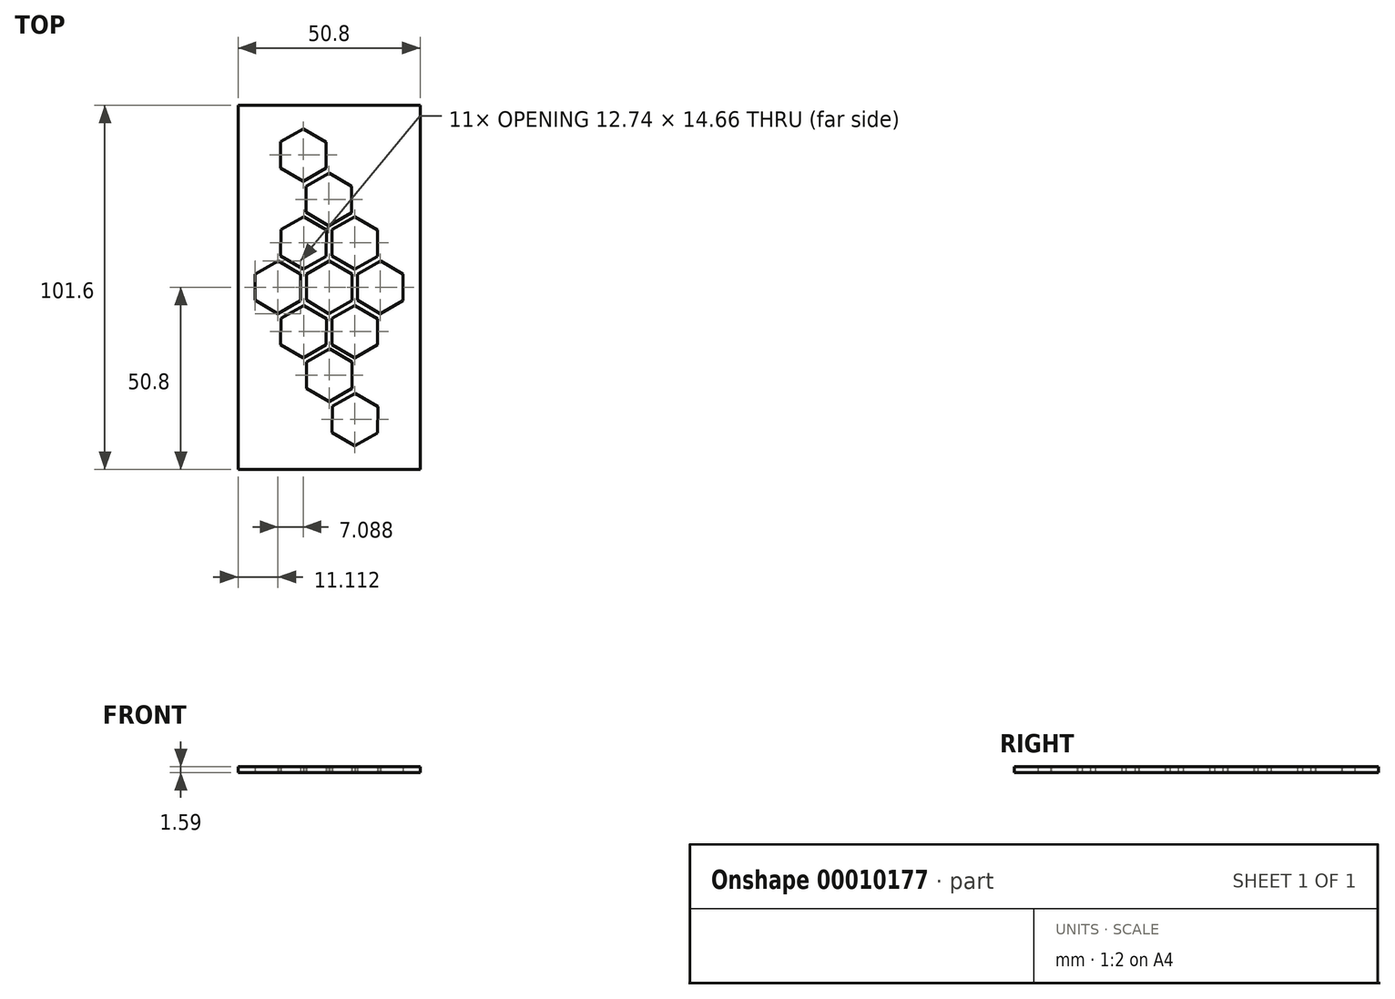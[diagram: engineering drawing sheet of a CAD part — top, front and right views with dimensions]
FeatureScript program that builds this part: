
annotation { "Feature Type Name" : "Feature", "Feature Type Description" : "" }
export const myFeature = defineFeature(function(context is Context, id is Id, definition is map)
    precondition{}
    {
        {
            var Q0;
            Q0=qCreatedBy(makeId("Top.planeOp"),FACE);
            var sketch = newSketch(context, id + "F0", { "sketchPlane" : qUnion([Q0])});
            skLineSegment(sketch, "E0.rect.bottom", {"start": v(25.4, 50.8) * mm, "end": v(-25.4, 50.8) * mm});
            skLineSegment(sketch, "E0.rect.top", {"start": v(25.4, -50.8) * mm, "end": v(-25.4, -50.8) * mm});
            skLineSegment(sketch, "E0.rect.left", {"start": v(25.4, 50.8) * mm, "end": v(25.4, -50.8) * mm});
            skLineSegment(sketch, "E0.rect.right", {"start": v(-25.4, 50.8) * mm, "end": v(-25.4, -50.8) * mm});
            skPoint(sketch, "E0.rect.middle", {"position": v(0, 0) * mm});
            skCircle(sketch, "E1.cCircle", {"center": v(0, 0) * mm, "radius": 6.35 * mm, "construction": true});
            skLineSegment(sketch, "E1.0", {"start": v(0.04, 7.33) * mm, "end": v(6.37, 3.63) * mm});
            skLineSegment(sketch, "E1.1", {"start": v(6.37, 3.63) * mm, "end": v(6.33, -3.7) * mm});
            skLineSegment(sketch, "E1.2", {"start": v(6.33, -3.7) * mm, "end": v(-0.04, -7.33) * mm});
            skLineSegment(sketch, "E1.3", {"start": v(-0.04, -7.33) * mm, "end": v(-6.37, -3.63) * mm});
            skLineSegment(sketch, "E1.4", {"start": v(-6.37, -3.63) * mm, "end": v(-6.33, 3.7) * mm});
            skLineSegment(sketch, "E1.5", {"start": v(-6.33, 3.7) * mm, "end": v(0.04, 7.33) * mm});
            skPoint(sketch, "E1.0.midPoint", {"position": v(3.2, 5.48) * mm});
            skCircle(sketch, "E2.1.0.0", {"center": v(14.29, 0) * mm, "radius": 6.35 * mm, "construction": true});
            skLineSegment(sketch, "E2.1.0.1", {"start": v(20.66, 3.63) * mm, "end": v(20.62, -3.7) * mm});
            skLineSegment(sketch, "E2.1.0.2", {"start": v(14.33, 7.33) * mm, "end": v(20.66, 3.63) * mm});
            skPoint(sketch, "E2.1.0.3", {"position": v(14.29, 0) * mm});
            skLineSegment(sketch, "E2.1.0.4", {"start": v(14.25, -7.33) * mm, "end": v(7.92, -3.63) * mm});
            skLineSegment(sketch, "E2.1.0.5", {"start": v(20.62, -3.7) * mm, "end": v(14.25, -7.33) * mm});
            skLineSegment(sketch, "E2.1.0.6", {"start": v(7.96, 3.7) * mm, "end": v(14.33, 7.33) * mm});
            skLineSegment(sketch, "E2.1.0.7", {"start": v(7.92, -3.63) * mm, "end": v(7.96, 3.7) * mm});
            skPoint(sketch, "E2.1.0.8", {"position": v(17.5, 5.48) * mm});
            skLineSegment(sketch, "E2.direction1", {"start": v(0, 0) * mm, "end": v(14.29, 0) * mm, "construction": true});
            skLineSegment(sketch, "E3.1.0", {"start": v(13.47, -16.07) * mm, "end": v(7.1, -19.7) * mm});
            skPoint(sketch, "E3.1.1", {"position": v(13.5, -12.4) * mm});
            skPoint(sketch, "E3.1.6", {"position": v(6.35, -0.03) * mm});
            skPoint(sketch, "E3.1.10", {"position": v(7.14, -12.37) * mm});
            skLineSegment(sketch, "E3.1.11", {"start": v(0.81, -8.67) * mm, "end": v(7.18, -5.04) * mm});
            skCircle(sketch, "E3.1.12", {"center": v(7.14, -12.37) * mm, "radius": 6.35 * mm, "construction": true});
            skLineSegment(sketch, "E3.1.14", {"start": v(0.77, -16) * mm, "end": v(0.81, -8.67) * mm});
            skLineSegment(sketch, "E3.1.15", {"start": v(7.1, -19.7) * mm, "end": v(0.77, -16) * mm});
            skLineSegment(sketch, "E3.1.16", {"start": v(13.51, -8.74) * mm, "end": v(13.47, -16.07) * mm});
            skLineSegment(sketch, "E3.1.17", {"start": v(7.18, -5.04) * mm, "end": v(13.51, -8.74) * mm});
            skLineSegment(sketch, "E3.1.18", {"start": v(0, 0) * mm, "end": v(7.14, -12.37) * mm, "construction": true});
            skLineSegment(sketch, "E3.2.0", {"start": v(-7.18, -19.7) * mm, "end": v(-13.51, -16) * mm});
            skPoint(sketch, "E3.2.1", {"position": v(-4, -17.89) * mm});
            skPoint(sketch, "E3.2.6", {"position": v(3.15, -5.52) * mm});
            skPoint(sketch, "E3.2.10", {"position": v(-7.14, -12.37) * mm});
            skLineSegment(sketch, "E3.2.11", {"start": v(-7.1, -5.04) * mm, "end": v(-0.77, -8.74) * mm});
            skCircle(sketch, "E3.2.12", {"center": v(-7.14, -12.37) * mm, "radius": 6.35 * mm, "construction": true});
            skLineSegment(sketch, "E3.2.14", {"start": v(-13.47, -8.67) * mm, "end": v(-7.1, -5.04) * mm});
            skLineSegment(sketch, "E3.2.15", {"start": v(-13.51, -16) * mm, "end": v(-13.47, -8.67) * mm});
            skLineSegment(sketch, "E3.2.16", {"start": v(-0.81, -16.07) * mm, "end": v(-7.18, -19.7) * mm});
            skLineSegment(sketch, "E3.2.17", {"start": v(-0.77, -8.74) * mm, "end": v(-0.81, -16.07) * mm});
            skLineSegment(sketch, "E3.2.18", {"start": v(0, 0) * mm, "end": v(-7.14, -12.37) * mm, "construction": true});
            skLineSegment(sketch, "E3.3.0", {"start": v(-20.66, -3.63) * mm, "end": v(-20.62, 3.7) * mm});
            skPoint(sketch, "E3.3.1", {"position": v(-17.5, -5.48) * mm});
            skPoint(sketch, "E3.3.6", {"position": v(-3.2, -5.48) * mm});
            skPoint(sketch, "E3.3.10", {"position": v(-14.29, 0) * mm});
            skLineSegment(sketch, "E3.3.11", {"start": v(-7.92, 3.63) * mm, "end": v(-7.96, -3.7) * mm});
            skCircle(sketch, "E3.3.12", {"center": v(-14.29, 0) * mm, "radius": 6.35 * mm, "construction": true});
            skLineSegment(sketch, "E3.3.14", {"start": v(-14.25, 7.33) * mm, "end": v(-7.92, 3.63) * mm});
            skLineSegment(sketch, "E3.3.15", {"start": v(-20.62, 3.7) * mm, "end": v(-14.25, 7.33) * mm});
            skLineSegment(sketch, "E3.3.16", {"start": v(-14.33, -7.33) * mm, "end": v(-20.66, -3.63) * mm});
            skLineSegment(sketch, "E3.3.17", {"start": v(-7.96, -3.7) * mm, "end": v(-14.33, -7.33) * mm});
            skLineSegment(sketch, "E3.3.18", {"start": v(0, 0) * mm, "end": v(-14.29, 0) * mm, "construction": true});
            skLineSegment(sketch, "E3.4.0", {"start": v(-13.47, 16.07) * mm, "end": v(-7.1, 19.7) * mm});
            skPoint(sketch, "E3.4.1", {"position": v(-13.5, 12.4) * mm});
            skPoint(sketch, "E3.4.6", {"position": v(-6.35, 0.03) * mm});
            skPoint(sketch, "E3.4.10", {"position": v(-7.14, 12.37) * mm});
            skLineSegment(sketch, "E3.4.11", {"start": v(-0.81, 8.67) * mm, "end": v(-7.18, 5.04) * mm});
            skCircle(sketch, "E3.4.12", {"center": v(-7.14, 12.37) * mm, "radius": 6.35 * mm, "construction": true});
            skLineSegment(sketch, "E3.4.14", {"start": v(-0.77, 16) * mm, "end": v(-0.81, 8.67) * mm});
            skLineSegment(sketch, "E3.4.15", {"start": v(-7.1, 19.7) * mm, "end": v(-0.77, 16) * mm});
            skLineSegment(sketch, "E3.4.16", {"start": v(-13.51, 8.74) * mm, "end": v(-13.47, 16.07) * mm});
            skLineSegment(sketch, "E3.4.17", {"start": v(-7.18, 5.04) * mm, "end": v(-13.51, 8.74) * mm});
            skLineSegment(sketch, "E3.4.18", {"start": v(0, 0) * mm, "end": v(-7.14, 12.37) * mm, "construction": true});
            skLineSegment(sketch, "E3.5.0", {"start": v(7.18, 19.7) * mm, "end": v(13.51, 16) * mm});
            skPoint(sketch, "E3.5.1", {"position": v(4, 17.89) * mm});
            skPoint(sketch, "E3.5.6", {"position": v(-3.15, 5.52) * mm});
            skPoint(sketch, "E3.5.10", {"position": v(7.14, 12.37) * mm});
            skLineSegment(sketch, "E3.5.11", {"start": v(7.1, 5.04) * mm, "end": v(0.77, 8.74) * mm});
            skCircle(sketch, "E3.5.12", {"center": v(7.14, 12.37) * mm, "radius": 6.35 * mm, "construction": true});
            skLineSegment(sketch, "E3.5.14", {"start": v(13.47, 8.67) * mm, "end": v(7.1, 5.04) * mm});
            skLineSegment(sketch, "E3.5.15", {"start": v(13.51, 16) * mm, "end": v(13.47, 8.67) * mm});
            skLineSegment(sketch, "E3.5.16", {"start": v(0.81, 16.07) * mm, "end": v(7.18, 19.7) * mm});
            skLineSegment(sketch, "E3.5.17", {"start": v(0.77, 8.74) * mm, "end": v(0.81, 16.07) * mm});
            skLineSegment(sketch, "E3.5.18", {"start": v(0, 0) * mm, "end": v(7.14, 12.37) * mm, "construction": true});
            skLineSegment(sketch, "E3.anchor1", {"start": v(0, 0) * mm, "end": v(20.62, -3.7) * mm, "construction": true});
            skLineSegment(sketch, "E3.anchor2", {"start": v(0, 0) * mm, "end": v(13.51, 16) * mm, "construction": true});
            skPoint(sketch, "E4.1.0.0", {"position": v(7.09, 36.9) * mm});
            skPoint(sketch, "E4.1.0.1", {"position": v(-13.55, 36.93) * mm});
            skLineSegment(sketch, "E4.1.0.2", {"start": v(-13.53, 40.6) * mm, "end": v(-7.16, 44.23) * mm});
            skLineSegment(sketch, "E4.1.0.3", {"start": v(-7.16, 44.23) * mm, "end": v(-0.83, 40.53) * mm});
            skPoint(sketch, "E4.1.0.4", {"position": v(3.94, 42.41) * mm});
            skLineSegment(sketch, "E4.1.0.5", {"start": v(7.13, 44.23) * mm, "end": v(13.46, 40.53) * mm});
            skLineSegment(sketch, "E4.1.0.6", {"start": v(0.76, 40.6) * mm, "end": v(7.13, 44.23) * mm});
            skLineSegment(sketch, "E4.1.0.7", {"start": v(-13.57, 33.26) * mm, "end": v(-13.53, 40.6) * mm});
            skLineSegment(sketch, "E4.1.0.8", {"start": v(-7.24, 29.56) * mm, "end": v(-13.57, 33.26) * mm});
            skLineSegment(sketch, "E4.1.0.9", {"start": v(-0.83, 40.53) * mm, "end": v(-0.87, 33.2) * mm});
            skLineSegment(sketch, "E4.1.0.10", {"start": v(-6.39, 28.22) * mm, "end": v(-0.02, 31.85) * mm});
            skLineSegment(sketch, "E4.1.0.11", {"start": v(-6.43, 20.9) * mm, "end": v(-6.39, 28.22) * mm});
            skLineSegment(sketch, "E4.1.0.12", {"start": v(-0.1, 17.19) * mm, "end": v(-6.43, 20.9) * mm});
            skLineSegment(sketch, "E4.1.0.13", {"start": v(6.27, 20.82) * mm, "end": v(-0.1, 17.19) * mm});
            skLineSegment(sketch, "E4.1.0.14", {"start": v(6.31, 28.15) * mm, "end": v(6.27, 20.82) * mm});
            skLineSegment(sketch, "E4.1.0.15", {"start": v(-0.02, 31.85) * mm, "end": v(6.31, 28.15) * mm});
            skLineSegment(sketch, "E4.1.0.16", {"start": v(-0.87, 33.2) * mm, "end": v(-7.24, 29.56) * mm});
            skLineSegment(sketch, "E4.1.0.17", {"start": v(0.72, 33.26) * mm, "end": v(0.76, 40.6) * mm});
            skLineSegment(sketch, "E4.1.0.18", {"start": v(7.05, 29.56) * mm, "end": v(0.72, 33.26) * mm});
            skLineSegment(sketch, "E4.1.0.19", {"start": v(13.42, 33.2) * mm, "end": v(7.05, 29.56) * mm});
            skLineSegment(sketch, "E4.1.0.20", {"start": v(13.46, 40.53) * mm, "end": v(13.42, 33.2) * mm});
            skLineSegment(sketch, "E4.direction1", {"start": v(7.14, 12.37) * mm, "end": v(7.09, 36.9) * mm, "construction": true});
            skLineSegment(sketch, "E5.1.2", {"start": v(6.43, -20.9) * mm, "end": v(6.39, -28.22) * mm});
            skLineSegment(sketch, "E5.1.3", {"start": v(0.1, -17.19) * mm, "end": v(6.43, -20.9) * mm});
            skLineSegment(sketch, "E5.1.4", {"start": v(-6.27, -20.82) * mm, "end": v(0.1, -17.19) * mm});
            skLineSegment(sketch, "E5.1.5", {"start": v(-6.31, -28.15) * mm, "end": v(-6.27, -20.82) * mm});
            skLineSegment(sketch, "E5.1.6", {"start": v(0.02, -31.85) * mm, "end": v(-6.31, -28.15) * mm});
            skLineSegment(sketch, "E5.1.7", {"start": v(6.39, -28.22) * mm, "end": v(0.02, -31.85) * mm});
            skLineSegment(sketch, "E5.1.8", {"start": v(7.24, -29.56) * mm, "end": v(13.57, -33.26) * mm});
            skLineSegment(sketch, "E5.1.9", {"start": v(0.87, -33.2) * mm, "end": v(7.24, -29.56) * mm});
            skLineSegment(sketch, "E5.1.10", {"start": v(0.83, -40.53) * mm, "end": v(0.87, -33.2) * mm});
            skLineSegment(sketch, "E5.1.11", {"start": v(7.16, -44.23) * mm, "end": v(0.83, -40.53) * mm});
            skLineSegment(sketch, "E5.1.12", {"start": v(13.53, -40.6) * mm, "end": v(7.16, -44.23) * mm});
            skLineSegment(sketch, "E5.1.13", {"start": v(13.57, -33.26) * mm, "end": v(13.53, -40.6) * mm});
            skLineSegment(sketch, "E5.1.14", {"start": v(-0.72, -33.26) * mm, "end": v(-0.76, -40.6) * mm});
            skLineSegment(sketch, "E5.1.15", {"start": v(-7.05, -29.56) * mm, "end": v(-0.72, -33.26) * mm});
            skLineSegment(sketch, "E5.1.16", {"start": v(-13.42, -33.2) * mm, "end": v(-7.05, -29.56) * mm});
            skLineSegment(sketch, "E5.1.17", {"start": v(-13.46, -40.53) * mm, "end": v(-13.42, -33.2) * mm});
            skLineSegment(sketch, "E5.1.18", {"start": v(-7.13, -44.23) * mm, "end": v(-13.46, -40.53) * mm});
            skLineSegment(sketch, "E5.1.19", {"start": v(-0.76, -40.6) * mm, "end": v(-7.13, -44.23) * mm});
            skLineSegment(sketch, "E6.1.0", {"start": v(27.58, 15.94) * mm, "end": v(27.54, 8.6) * mm});
            skLineSegment(sketch, "E6.1.2", {"start": v(-34.72, -28.31) * mm, "end": v(-34.68, -20.98) * mm});
            skLineSegment(sketch, "E6.1.3", {"start": v(-41.83, -8.6) * mm, "end": v(-35.46, -4.98) * mm});
            skLineSegment(sketch, "E6.1.4", {"start": v(29.17, 16.01) * mm, "end": v(35.54, 19.64) * mm});
            skLineSegment(sketch, "E6.1.6", {"start": v(-14.84, -8.68) * mm, "end": v(-14.88, -16.01) * mm});
            skLineSegment(sketch, "E6.1.9", {"start": v(-21.25, -19.64) * mm, "end": v(-27.58, -15.94) * mm});
            skLineSegment(sketch, "E6.1.10", {"start": v(21.17, 4.98) * mm, "end": v(14.84, 8.68) * mm});
            skLineSegment(sketch, "E6.1.17", {"start": v(-14.29, 0) * mm, "end": v(-35.5, -12.3) * mm, "construction": true});
            skLineSegment(sketch, "E6.1.18", {"start": v(-41.87, -15.94) * mm, "end": v(-41.83, -8.6) * mm});
            skLineSegment(sketch, "E6.1.19", {"start": v(29.13, 8.68) * mm, "end": v(29.17, 16.01) * mm});
            skLineSegment(sketch, "E6.1.22", {"start": v(-14.88, -16.01) * mm, "end": v(-21.25, -19.64) * mm});
            skLineSegment(sketch, "E6.1.23", {"start": v(27.54, 8.6) * mm, "end": v(21.17, 4.98) * mm});
            skPoint(sketch, "E6.1.27", {"position": v(-35.5, -12.3) * mm});
            skLineSegment(sketch, "E6.1.34", {"start": v(-27.54, -8.6) * mm, "end": v(-21.17, -4.98) * mm});
            skLineSegment(sketch, "E6.1.36", {"start": v(21.98, 21.05) * mm, "end": v(22.02, 28.38) * mm});
            skPoint(sketch, "E6.1.37", {"position": v(-38.7, -17.8) * mm});
            skLineSegment(sketch, "E6.1.41", {"start": v(-28.31, -17.35) * mm, "end": v(-21.98, -21.05) * mm});
            skLineSegment(sketch, "E6.1.42", {"start": v(34.68, 20.98) * mm, "end": v(28.31, 17.35) * mm});
            skLineSegment(sketch, "E6.1.44", {"start": v(41.83, 8.6) * mm, "end": v(35.46, 4.98) * mm});
            skLineSegment(sketch, "E6.1.52", {"start": v(-21.17, -4.98) * mm, "end": v(-14.84, -8.68) * mm});
            skLineSegment(sketch, "E6.1.53", {"start": v(21.25, 19.64) * mm, "end": v(27.58, 15.94) * mm});
            skLineSegment(sketch, "E6.1.57", {"start": v(35.46, 4.98) * mm, "end": v(29.13, 8.68) * mm});
            skLineSegment(sketch, "E6.1.62", {"start": v(-29.17, -16.01) * mm, "end": v(-35.54, -19.64) * mm});
            skLineSegment(sketch, "E6.1.63", {"start": v(0, 0) * mm, "end": v(-7.1, 19.7) * mm, "construction": true});
            skLineSegment(sketch, "E6.1.64", {"start": v(34.72, 28.31) * mm, "end": v(34.68, 20.98) * mm});
            skLineSegment(sketch, "E6.1.71", {"start": v(-27.58, -15.94) * mm, "end": v(-27.54, -8.6) * mm});
            skLineSegment(sketch, "E6.1.72", {"start": v(28.31, 17.35) * mm, "end": v(21.98, 21.05) * mm});
            skPoint(sketch, "E6.1.73", {"position": v(-25.2, -30.2) * mm});
            skLineSegment(sketch, "E6.1.75", {"start": v(28.4, 32.02) * mm, "end": v(34.72, 28.31) * mm});
            skLineSegment(sketch, "E6.1.76", {"start": v(-29.13, -8.68) * mm, "end": v(-29.17, -16.01) * mm});
            skLineSegment(sketch, "E6.1.77", {"start": v(0, 0) * mm, "end": v(-20.62, 3.7) * mm, "construction": true});
            skLineSegment(sketch, "E6.1.85", {"start": v(22.02, 28.38) * mm, "end": v(28.4, 32.02) * mm});
            skLineSegment(sketch, "E6.1.86", {"start": v(-35.46, -4.98) * mm, "end": v(-29.13, -8.68) * mm});
            skLineSegment(sketch, "E6.1.87", {"start": v(-28.4, -32.02) * mm, "end": v(-34.72, -28.31) * mm});
            skLineSegment(sketch, "E6.1.89", {"start": v(-34.68, -20.98) * mm, "end": v(-28.31, -17.35) * mm});
            skLineSegment(sketch, "E6.1.90", {"start": v(14.84, 8.68) * mm, "end": v(14.88, 16.01) * mm});
            skLineSegment(sketch, "E6.1.91", {"start": v(35.54, 19.64) * mm, "end": v(41.87, 15.94) * mm});
            skLineSegment(sketch, "E6.1.92", {"start": v(14.88, 16.01) * mm, "end": v(21.25, 19.64) * mm});
            skLineSegment(sketch, "E6.1.93", {"start": v(-21.98, -21.05) * mm, "end": v(-22.02, -28.38) * mm});
            skLineSegment(sketch, "E6.1.94", {"start": v(41.87, 15.94) * mm, "end": v(41.83, 8.6) * mm});
            skLineSegment(sketch, "E6.1.107", {"start": v(-22.02, -28.38) * mm, "end": v(-28.4, -32.02) * mm});
            skLineSegment(sketch, "E6.1.108", {"start": v(-35.54, -19.64) * mm, "end": v(-41.87, -15.94) * mm});
            skLineSegment(sketch, "E6.2.0", {"start": v(-27.6, 15.91) * mm, "end": v(-21.22, 19.54) * mm});
            skLineSegment(sketch, "E6.2.2", {"start": v(41.88, -15.91) * mm, "end": v(35.51, -19.54) * mm});
            skLineSegment(sketch, "E6.2.3", {"start": v(28.37, -31.92) * mm, "end": v(22.04, -28.22) * mm});
            skLineSegment(sketch, "E6.2.4", {"start": v(-28.45, 17.25) * mm, "end": v(-34.78, 20.95) * mm});
            skLineSegment(sketch, "E6.2.6", {"start": v(14.93, -8.51) * mm, "end": v(21.3, -4.88) * mm});
            skLineSegment(sketch, "E6.2.9", {"start": v(27.63, -8.58) * mm, "end": v(27.6, -15.91) * mm});
            skLineSegment(sketch, "E6.2.10", {"start": v(-14.9, 15.84) * mm, "end": v(-14.93, 8.51) * mm});
            skLineSegment(sketch, "E6.2.17", {"start": v(7.14, -12.37) * mm, "end": v(28.4, -24.59) * mm, "construction": true});
            skLineSegment(sketch, "E6.2.18", {"start": v(34.74, -28.29) * mm, "end": v(28.37, -31.92) * mm});
            skLineSegment(sketch, "E6.2.19", {"start": v(-22.08, 20.89) * mm, "end": v(-28.45, 17.25) * mm});
            skLineSegment(sketch, "E6.2.22", {"start": v(21.3, -4.88) * mm, "end": v(27.63, -8.58) * mm});
            skLineSegment(sketch, "E6.2.23", {"start": v(-21.22, 19.54) * mm, "end": v(-14.9, 15.84) * mm});
            skPoint(sketch, "E6.2.27", {"position": v(28.4, -24.59) * mm});
            skLineSegment(sketch, "E6.2.34", {"start": v(21.22, -19.54) * mm, "end": v(14.9, -15.84) * mm});
            skLineSegment(sketch, "E6.2.36", {"start": v(-29.22, 8.51) * mm, "end": v(-35.6, 4.88) * mm});
            skPoint(sketch, "E6.2.37", {"position": v(34.76, -24.62) * mm});
            skLineSegment(sketch, "E6.2.41", {"start": v(29.18, -15.84) * mm, "end": v(29.22, -8.51) * mm});
            skLineSegment(sketch, "E6.2.42", {"start": v(-35.51, 19.54) * mm, "end": v(-29.18, 15.84) * mm});
            skLineSegment(sketch, "E6.2.44", {"start": v(-28.37, 31.92) * mm, "end": v(-22.04, 28.22) * mm});
            skLineSegment(sketch, "E6.2.52", {"start": v(14.9, -15.84) * mm, "end": v(14.93, -8.51) * mm});
            skLineSegment(sketch, "E6.2.53", {"start": v(-27.63, 8.58) * mm, "end": v(-27.6, 15.91) * mm});
            skLineSegment(sketch, "E6.2.57", {"start": v(-22.04, 28.22) * mm, "end": v(-22.08, 20.89) * mm});
            skLineSegment(sketch, "E6.2.62", {"start": v(28.45, -17.25) * mm, "end": v(34.78, -20.95) * mm});
            skLineSegment(sketch, "E6.2.63", {"start": v(0, 0) * mm, "end": v(-13.51, -16) * mm, "construction": true});
            skLineSegment(sketch, "E6.2.64", {"start": v(-41.88, 15.91) * mm, "end": v(-35.51, 19.54) * mm});
            skLineSegment(sketch, "E6.2.71", {"start": v(27.6, -15.91) * mm, "end": v(21.22, -19.54) * mm});
            skLineSegment(sketch, "E6.2.72", {"start": v(-29.18, 15.84) * mm, "end": v(-29.22, 8.51) * mm});
            skPoint(sketch, "E6.2.73", {"position": v(38.76, -6.73) * mm});
            skLineSegment(sketch, "E6.2.75", {"start": v(-41.92, 8.58) * mm, "end": v(-41.88, 15.91) * mm});
            skLineSegment(sketch, "E6.2.76", {"start": v(22.08, -20.89) * mm, "end": v(28.45, -17.25) * mm});
            skLineSegment(sketch, "E6.2.77", {"start": v(0, 0) * mm, "end": v(7.1, -19.7) * mm, "construction": true});
            skLineSegment(sketch, "E6.2.85", {"start": v(-35.6, 4.88) * mm, "end": v(-41.92, 8.58) * mm});
            skLineSegment(sketch, "E6.2.86", {"start": v(22.04, -28.22) * mm, "end": v(22.08, -20.89) * mm});
            skLineSegment(sketch, "E6.2.87", {"start": v(41.92, -8.58) * mm, "end": v(41.88, -15.91) * mm});
            skLineSegment(sketch, "E6.2.89", {"start": v(35.51, -19.54) * mm, "end": v(29.18, -15.84) * mm});
            skLineSegment(sketch, "E6.2.90", {"start": v(-14.93, 8.51) * mm, "end": v(-21.3, 4.88) * mm});
            skLineSegment(sketch, "E6.2.91", {"start": v(-34.78, 20.95) * mm, "end": v(-34.74, 28.29) * mm});
            skLineSegment(sketch, "E6.2.92", {"start": v(-21.3, 4.88) * mm, "end": v(-27.63, 8.58) * mm});
            skLineSegment(sketch, "E6.2.93", {"start": v(29.22, -8.51) * mm, "end": v(35.6, -4.88) * mm});
            skLineSegment(sketch, "E6.2.94", {"start": v(-34.74, 28.29) * mm, "end": v(-28.37, 31.92) * mm});
            skLineSegment(sketch, "E6.2.107", {"start": v(35.6, -4.88) * mm, "end": v(41.92, -8.58) * mm});
            skLineSegment(sketch, "E6.2.108", {"start": v(34.78, -20.95) * mm, "end": v(34.74, -28.29) * mm});
            skLineSegment(sketch, "E7", {"start": v(7.05, 29.56) * mm, "end": v(14.88, 16.01) * mm});
            skLineSegment(sketch, "E8", {"start": v(-6.31, -28.15) * mm, "end": v(-14.88, -16.01) * mm});
            skSolve(sketch);
        }
        {
            var Q0;
            {var subQ6=sQuery(id+"F0.wireOp",EDGE,"E6.1.10");Q0=makeQuery(id+"F0.imprint","IMPRINT",FACE,{"disambiguationData":[TD([[makeQuery(id+"F0.imprint","IMPRINT",EDGE,{"derivedFrom":subQ6}),-1.0]])]});}
            var Q1;
            {var subQ0=sQuery(id+"F0.wireOp",EDGE,"E6.2.57");Q1=makeQuery(id+"F0.imprint","IMPRINT",FACE,{"disambiguationData":[TD([[makeQuery(id+"F0.imprint","IMPRINT",EDGE,{"derivedFrom":subQ0}),-1.0]])]});}
            var Q2;
            Q2=makeQuery(id+"F0.imprint","IMPRINT",FACE,{"disambiguationData":[TD([[makeQuery(id+"F0.imprint","IMPRINT",EDGE,{"derivedFrom":sQuery(id+"F0.wireOp",EDGE,"E6.1.6")}),-1.0]])]});
            var Q3;
            {var subQ12=sQuery(id+"F0.wireOp",EDGE,"E0.rect.bottom");Q3=makeQuery(id+"F0.imprint","IMPRINT",FACE,{"disambiguationData":[TD([[makeQuery(id+"F0.imprint","IMPRINT",EDGE,{"derivedFrom":subQ12}),1.0]])]});}
            var Q4;
            Q4=makeQuery(id+"F0.imprint","IMPRINT",FACE,{"disambiguationData":[TD([[makeQuery(id+"F0.imprint","IMPRINT",EDGE,{"derivedFrom":sQuery(id+"F0.wireOp",EDGE,"E6.2.10")}),-1.0]])]});
            var Q5;
            {var subQ3=sQuery(id+"F0.wireOp",EDGE,"E6.1.93");Q5=makeQuery(id+"F0.imprint","IMPRINT",FACE,{"disambiguationData":[TD([[makeQuery(id+"F0.imprint","IMPRINT",EDGE,{"derivedFrom":subQ3}),-1.0]])]});}
            var Q6;
            {var subQ0=sQuery(id+"F0.wireOp",EDGE,"E6.2.86");Q6=makeQuery(id+"F0.imprint","IMPRINT",FACE,{"disambiguationData":[TD([[makeQuery(id+"F0.imprint","IMPRINT",EDGE,{"derivedFrom":subQ0}),-1.0]])]});}
            var Q7;
            {var subQ6=sQuery(id+"F0.wireOp",EDGE,"E6.2.6");Q7=makeQuery(id+"F0.imprint","IMPRINT",FACE,{"disambiguationData":[TD([[makeQuery(id+"F0.imprint","IMPRINT",EDGE,{"derivedFrom":subQ6}),-1.0]])]});}
            var Q8;
            {var subQ3=sQuery(id+"F0.wireOp",EDGE,"E6.1.36");Q8=makeQuery(id+"F0.imprint","IMPRINT",FACE,{"disambiguationData":[TD([[makeQuery(id+"F0.imprint","IMPRINT",EDGE,{"derivedFrom":subQ3}),-1.0]])]});}
            var Q9;
            Q9=makeQuery(id+"F0.imprint","IMPRINT",FACE,{"disambiguationData":[TD([[makeQuery(id+"F0.imprint","IMPRINT",EDGE,{"derivedFrom":sQuery(id+"F0.wireOp",EDGE,"E4.1.0.5")}),-1.0]])]});
            var Q10;
            Q10=makeQuery(id+"F0.imprint","IMPRINT",FACE,{"disambiguationData":[TD([[makeQuery(id+"F0.imprint","IMPRINT",EDGE,{"derivedFrom":sQuery(id+"F0.wireOp",EDGE,"E5.1.14")}),-1.0]])]});
            extrude(context, id + "F1", {"entities" : qUnion([Q0, Q1, Q2, Q3, Q4, Q5, Q6, Q7, Q8, Q9, Q10]), "depth" : 1.59 * mm});
        }
    });
